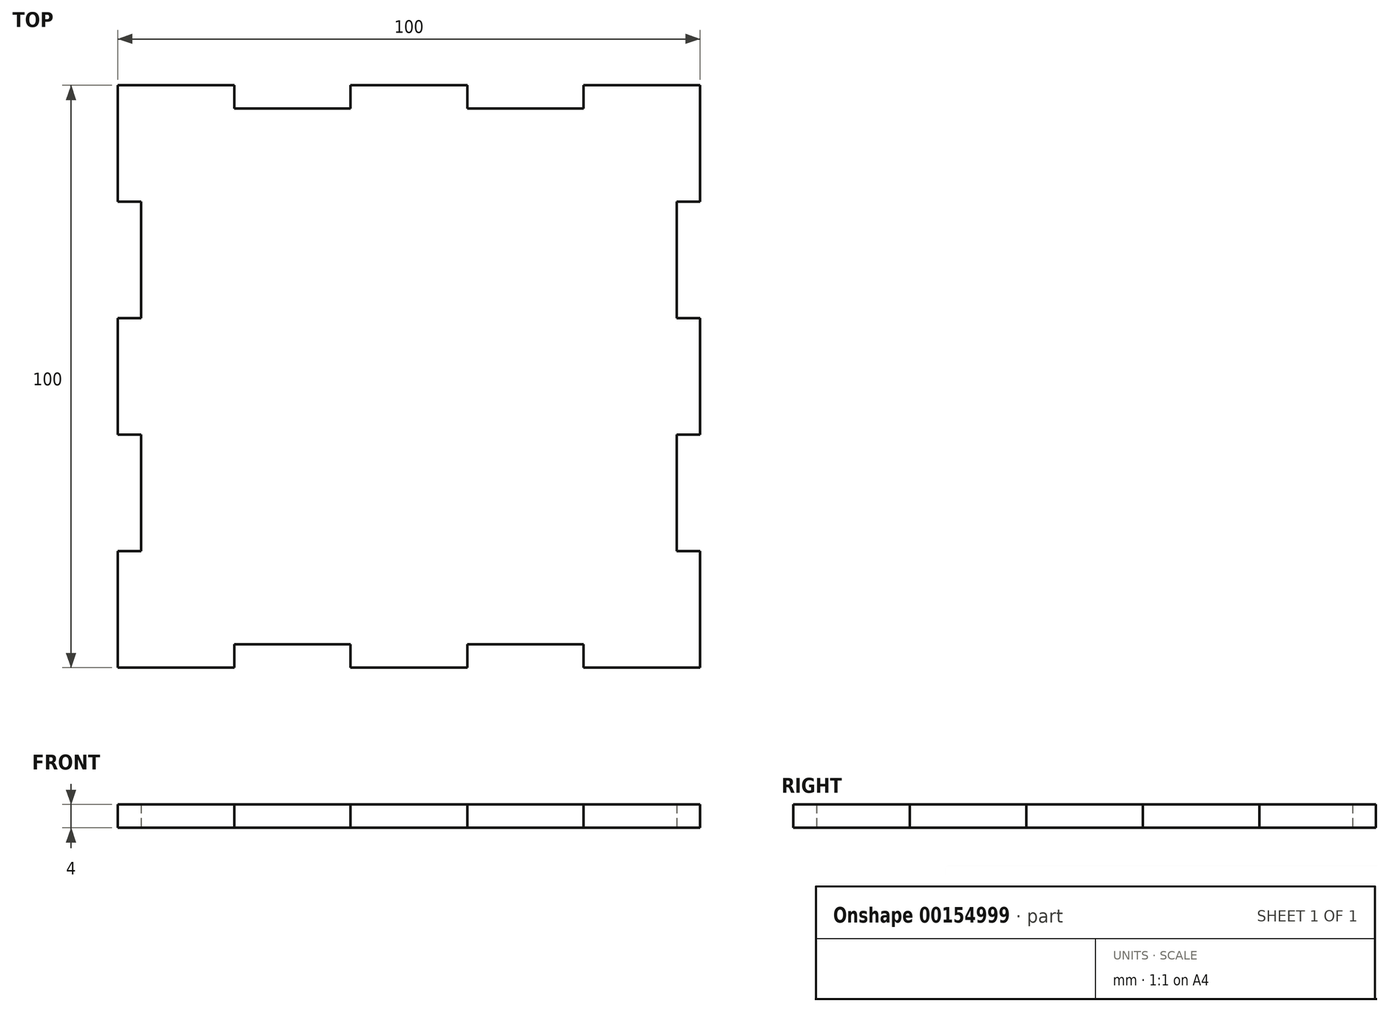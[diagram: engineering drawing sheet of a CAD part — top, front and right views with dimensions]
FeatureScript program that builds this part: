
annotation { "Feature Type Name" : "Feature", "Feature Type Description" : "" }
export const myFeature = defineFeature(function(context is Context, id is Id, definition is map)
    precondition{}
    {
        {
            var Q0;
            Q0=qCreatedBy(makeId("Top.planeOp"),FACE);
            var sketch = newSketch(context, id + "F0", { "sketchPlane" : qUnion([Q0])});
            skLineSegment(sketch, "E0.bottom", {"start": v(0, 100) * mm, "end": v(100, 100) * mm});
            skLineSegment(sketch, "E0.top", {"start": v(0, 0) * mm, "end": v(100, 0) * mm});
            skLineSegment(sketch, "E0.left", {"start": v(0, 100) * mm, "end": v(0, 0) * mm});
            skLineSegment(sketch, "E0.right", {"start": v(100, 100) * mm, "end": v(100, 0) * mm});
            skLineSegment(sketch, "E1.bottom", {"start": v(20, 4) * mm, "end": v(40, 4) * mm});
            skLineSegment(sketch, "E1.top", {"start": v(20, 0) * mm, "end": v(40, 0) * mm});
            skLineSegment(sketch, "E1.left", {"start": v(20, 4) * mm, "end": v(20, 0) * mm});
            skLineSegment(sketch, "E1.right", {"start": v(40, 4) * mm, "end": v(40, 0) * mm});
            skLineSegment(sketch, "E2.bottom", {"start": v(60, 4) * mm, "end": v(80, 4) * mm});
            skLineSegment(sketch, "E2.top", {"start": v(60, 0) * mm, "end": v(80, 0) * mm});
            skLineSegment(sketch, "E2.left", {"start": v(60, 4) * mm, "end": v(60, 0) * mm});
            skLineSegment(sketch, "E2.right", {"start": v(80, 4) * mm, "end": v(80, 0) * mm});
            skLineSegment(sketch, "E3.bottom", {"start": v(96, 80) * mm, "end": v(100, 80) * mm});
            skLineSegment(sketch, "E3.top", {"start": v(96, 60) * mm, "end": v(100, 60) * mm});
            skLineSegment(sketch, "E3.left", {"start": v(96, 80) * mm, "end": v(96, 60) * mm});
            skLineSegment(sketch, "E3.right", {"start": v(100, 80) * mm, "end": v(100, 60) * mm});
            skLineSegment(sketch, "E4.bottom", {"start": v(96, 40) * mm, "end": v(100, 40) * mm});
            skLineSegment(sketch, "E4.top", {"start": v(96, 20) * mm, "end": v(100, 20) * mm});
            skLineSegment(sketch, "E4.left", {"start": v(96, 40) * mm, "end": v(96, 20) * mm});
            skLineSegment(sketch, "E4.right", {"start": v(100, 40) * mm, "end": v(100, 20) * mm});
            skLineSegment(sketch, "E5.bottom", {"start": v(0, 40) * mm, "end": v(4, 40) * mm});
            skLineSegment(sketch, "E5.top", {"start": v(0, 20) * mm, "end": v(4, 20) * mm});
            skLineSegment(sketch, "E5.left", {"start": v(0, 40) * mm, "end": v(0, 20) * mm});
            skLineSegment(sketch, "E5.right", {"start": v(4, 40) * mm, "end": v(4, 20) * mm});
            skLineSegment(sketch, "E6.bottom", {"start": v(0, 80) * mm, "end": v(4, 80) * mm});
            skLineSegment(sketch, "E6.top", {"start": v(0, 60) * mm, "end": v(4, 60) * mm});
            skLineSegment(sketch, "E6.left", {"start": v(0, 80) * mm, "end": v(0, 60) * mm});
            skLineSegment(sketch, "E6.right", {"start": v(4, 80) * mm, "end": v(4, 60) * mm});
            skLineSegment(sketch, "E7.bottom", {"start": v(20, 100) * mm, "end": v(40, 100) * mm});
            skLineSegment(sketch, "E7.top", {"start": v(20, 96) * mm, "end": v(40, 96) * mm});
            skLineSegment(sketch, "E7.left", {"start": v(20, 100) * mm, "end": v(20, 96) * mm});
            skLineSegment(sketch, "E7.right", {"start": v(40, 100) * mm, "end": v(40, 96) * mm});
            skLineSegment(sketch, "E8.bottom", {"start": v(60, 100) * mm, "end": v(80, 100) * mm});
            skLineSegment(sketch, "E8.top", {"start": v(60, 96) * mm, "end": v(80, 96) * mm});
            skLineSegment(sketch, "E8.left", {"start": v(60, 100) * mm, "end": v(60, 96) * mm});
            skLineSegment(sketch, "E8.right", {"start": v(80, 100) * mm, "end": v(80, 96) * mm});
            skSolve(sketch);
        }
        {
            var Q0;
            Q0=makeQuery(id+"F0.imprint","IMPRINT",FACE,{"disambiguationData":[TD([[makeQuery(id+"F0.imprint","IMPRINT",EDGE,{"derivedFrom":sQuery(id+"F0.wireOp",EDGE,"E1.bottom")}),1.0]])]});
            extrude(context, id + "F1", {"entities" : qUnion([Q0]), "depth" : 4 * mm});
        }
    });
